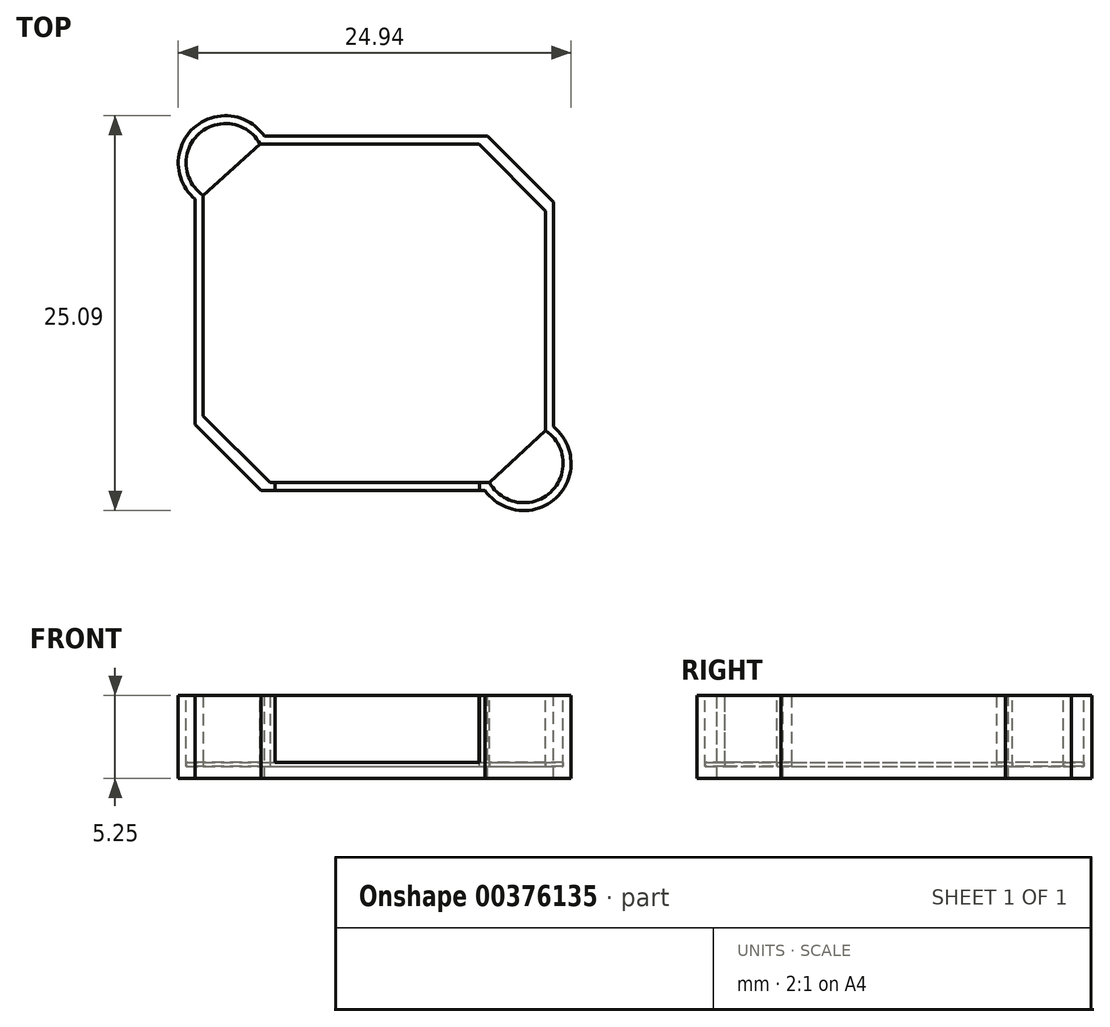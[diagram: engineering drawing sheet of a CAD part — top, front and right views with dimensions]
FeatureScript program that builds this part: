
annotation { "Feature Type Name" : "Feature", "Feature Type Description" : "" }
export const myFeature = defineFeature(function(context is Context, id is Id, definition is map)
    precondition{}
    {
        {
            var Q0;
            Q0=qCreatedBy(makeId("Top.planeOp"),FACE);
            var sketch = newSketch(context, id + "F0", { "sketchPlane" : qUnion([Q0])});
            skLineSegment(sketch, "E0.bottom", {"start": v(11.06, 7.36) * mm, "end": v(32.81, 7.36) * mm});
            skLineSegment(sketch, "E0.top", {"start": v(11.06, 28.86) * mm, "end": v(32.81, 28.86) * mm});
            skLineSegment(sketch, "E0.left", {"start": v(11.06, 7.36) * mm, "end": v(11.06, 28.86) * mm});
            skLineSegment(sketch, "E0.right", {"start": v(32.81, 7.36) * mm, "end": v(32.81, 28.86) * mm});
            skSolve(sketch);
        }
        {
            var Q0;
            Q0=makeQuery(id+"F0.imprint","IMPRINT",FACE,{"disambiguationData":[TD([[makeQuery(id+"F0.imprint","IMPRINT",EDGE,{"derivedFrom":sQuery(id+"F0.wireOp",EDGE,"E0.bottom")}),1.0]])]});
            extrude(context, id + "F1", {"entities" : qUnion([Q0]), "depth" : 6.5 * mm, "offsetDistance" : 25 * mm});
        }
        {
            var Q0;
            Q0=makeQuery(id+"F1.opExtrude","CAP_FACE",FACE,{"disambiguationData":[OSD([sQuery(id+"F0.wireOp",EDGE,"E0.bottom"),sQuery(id+"F0.wireOp",EDGE,"E0.top"),sQuery(id+"F0.wireOp",EDGE,"E0.left"),sQuery(id+"F0.wireOp",EDGE,"E0.right")])],"isStart":false});
            var sketch = newSketch(context, id + "F2", { "sketchPlane" : qUnion([Q0])});
            skCircle(sketch, "E1", {"center": v(12.48, 27.67) * mm, "radius": 2.5 * mm});
            skCircle(sketch, "E2", {"center": v(31.42, 8.58) * mm, "radius": 2.5 * mm});
            skSolve(sketch);
        }
        {
            var Q0;
            Q0 = qSketchRegion(id + "F2", true);
            var Q1;
            Q1=makeQuery(id+"F1.opExtrude","CAP_FACE",FACE,{"disambiguationData":[OSD([sQuery(id+"F0.wireOp",EDGE,"E0.bottom"),sQuery(id+"F0.wireOp",EDGE,"E0.top"),sQuery(id+"F0.wireOp",EDGE,"E0.left"),sQuery(id+"F0.wireOp",EDGE,"E0.right")])],"isStart":true});
            extrude(context, id + "F3", {"entities" : qUnion([Q0]), "operationType" : NewBodyOperationType.ADD, "endBound" : BoundingType.UP_TO_SURFACE, "oppositeDirection" : true, "endBoundEntityFace" : qUnion([Q1]), "depth" : 25 * mm});
        }
        {
            var Q0;
            {var subQ0=sQuery(id+"F0.wireOp",EDGE,"E0.right");var subQ1=sQuery(id+"F0.wireOp",EDGE,"E0.top");var subQ2=sQuery(id+"F0.wireOp",EDGE,"E0.left");var subQ3=sQuery(id+"F0.wireOp",EDGE,"E0.bottom");Q0=makeQuery(id+"F3.boolean.opBoolean","MERGE",FACE,{"derivedFrom":[makeQuery(id+"F1.opExtrude","CAP_FACE",FACE,{"disambiguationData":[OSD([subQ3,subQ1,subQ2,subQ0])],"isStart":false}),makeQuery(id+"F3.opExtrude","CAP_FACE",FACE,{"disambiguationData":[OSD([subQ3,subQ2,sQuery(id+"F2.wireOp",EDGE,"4af49626-d3c6-4b5d-b80f-25b6aeb158dc")])],"isStart":true}),makeQuery(id+"F3.opExtrude","CAP_FACE",FACE,{"disambiguationData":[OSD([subQ1,subQ0,sQuery(id+"F2.wireOp",EDGE,"7a161d0c-e22c-40a0-a662-b902da0d4264")])],"isStart":true})]});}
            var Q1;
            Q1=makeQuery(id+"F1.opExtrude","SWEPT_BODY",BODY,{"disambiguationData":[OSD([sQuery(id+"F0.wireOp",EDGE,"E0.bottom"),sQuery(id+"F0.wireOp",EDGE,"E0.top"),sQuery(id+"F0.wireOp",EDGE,"E0.left"),sQuery(id+"F0.wireOp",EDGE,"E0.right")])]});
            shell(context, id + "F4", {"entities" : qUnion([Q0]), "parts" : qUnion([Q1]), "thickness" : 0.5 * mm, "oppositeDirection" : true});
        }
        {
            var Q0;
            Q0=makeQuery(id+"F0.imprint","IMPRINT",FACE,{"disambiguationData":[TD([[makeQuery(id+"F0.imprint","IMPRINT",EDGE,{"derivedFrom":sQuery(id+"F0.wireOp",EDGE,"E0.bottom")}),1.0]])]});
            var sketch = newSketch(context, id + "F5", { "sketchPlane" : qUnion([Q0])});
            skCircle(sketch, "E3", {"center": v(21.94, 18.1) * mm, "radius": 6 * mm});
            skLineSegment(sketch, "E4", {"start": v(32.81, 18.1) * mm, "end": v(11.06, 18.1) * mm});
            skSolve(sketch);
        }
        {
            var Q0;
            Q0=makeQuery(id+"F3.boolean.opBoolean","MERGE",FACE,{"derivedFrom":[makeQuery(id+"F1.opExtrude","CAP_FACE",FACE,{"disambiguationData":[OSD([sQuery(id+"F0.wireOp",EDGE,"E0.bottom"),sQuery(id+"F0.wireOp",EDGE,"E0.top"),sQuery(id+"F0.wireOp",EDGE,"E0.left"),sQuery(id+"F0.wireOp",EDGE,"E0.right")])],"isStart":false}),makeQuery(id+"F3.opExtrude","CAP_FACE",FACE,{"disambiguationData":[OSD([sQuery(id+"F2.wireOp",EDGE,"E1")])],"isStart":true}),makeQuery(id+"F3.opExtrude","CAP_FACE",FACE,{"disambiguationData":[OSD([sQuery(id+"F2.wireOp",EDGE,"E2")])],"isStart":true})]});
            var sketch = newSketch(context, id + "F6", { "sketchPlane" : qUnion([Q0])});
            skLineSegment(sketch, "E5", {"start": v(32.81, 10.66) * mm, "end": v(32.81, 5.92) * mm});
            skLineSegment(sketch, "E6", {"start": v(32.81, 5.92) * mm, "end": v(37.54, 5.92) * mm});
            skLineSegment(sketch, "E7", {"start": v(37.54, 5.92) * mm, "end": v(37.54, 10.66) * mm});
            skLineSegment(sketch, "E8", {"start": v(37.54, 10.66) * mm, "end": v(32.81, 10.66) * mm});
            skLineSegment(sketch, "E9", {"start": v(32.81, 10.66) * mm, "end": v(32.81, 10.66) * mm});
            skSolve(sketch);
        }
        {
            var Q0;
            Q0=makeQuery(id+"F0.imprint","IMPRINT",FACE,{"disambiguationData":[TD([[makeQuery(id+"F0.imprint","IMPRINT",EDGE,{"derivedFrom":sQuery(id+"F0.wireOp",EDGE,"E0.bottom")}),1.0]])]});
            var sketch = newSketch(context, id + "F7", { "sketchPlane" : qUnion([Q0])});
            skLineSegment(sketch, "E10", {"start": v(11.06, 11.6) * mm, "end": v(15.3, 7.36) * mm});
            skLineSegment(sketch, "E11", {"start": v(11.06, 10.54) * mm, "end": v(14.24, 7.36) * mm});
            skLineSegment(sketch, "E12", {"start": v(11.06, 10.54) * mm, "end": v(11.06, 11.6) * mm});
            skLineSegment(sketch, "E13", {"start": v(14.24, 7.36) * mm, "end": v(15.3, 7.36) * mm});
            skLineSegment(sketch, "E14", {"start": v(28.57, 28.86) * mm, "end": v(32.81, 24.61) * mm});
            skLineSegment(sketch, "E15", {"start": v(29.63, 28.86) * mm, "end": v(32.81, 25.68) * mm});
            skSolve(sketch);
        }
        {
            var Q0;
            Q0 = qSketchRegion(id + "F7", true);
            var Q1;
            {var subQ0=sQuery(id+"F7.wireOp",EDGE,"E14");Q1=makeQuery(id+"F7.imprint","IMPRINT",FACE,{"disambiguationData":[TD([[makeQuery(id+"F7.imprint","IMPRINT",EDGE,{"derivedFrom":subQ0}),1.0]])]});}
            var Q2;
            Q2=makeQuery(id+"F3.boolean.opBoolean","MERGE",FACE,{"derivedFrom":[makeQuery(id+"F1.opExtrude","CAP_FACE",FACE,{"disambiguationData":[OSD([sQuery(id+"F0.wireOp",EDGE,"E0.bottom"),sQuery(id+"F0.wireOp",EDGE,"E0.top"),sQuery(id+"F0.wireOp",EDGE,"E0.left"),sQuery(id+"F0.wireOp",EDGE,"E0.right")])],"isStart":false}),makeQuery(id+"F3.opExtrude","CAP_FACE",FACE,{"disambiguationData":[OSD([sQuery(id+"F2.wireOp",EDGE,"E1")])],"isStart":true}),makeQuery(id+"F3.opExtrude","CAP_FACE",FACE,{"disambiguationData":[OSD([sQuery(id+"F2.wireOp",EDGE,"E2")])],"isStart":true})]});
            extrude(context, id + "F8", {"entities" : qUnion([Q0, Q1]), "operationType" : NewBodyOperationType.ADD, "endBound" : BoundingType.UP_TO_SURFACE, "endBoundEntityFace" : qUnion([Q2]), "depth" : 25 * mm});
        }
        {
            var Q0;
            {var subQ0=sQuery(id+"F2.wireOp",EDGE,"E2");var subQ1=sQuery(id+"F2.wireOp",EDGE,"E1");var subQ2=sQuery(id+"F0.wireOp",EDGE,"E0.right");var subQ3=sQuery(id+"F0.wireOp",EDGE,"E0.left");var subQ4=sQuery(id+"F0.wireOp",EDGE,"E0.top");var subQ5=sQuery(id+"F0.wireOp",EDGE,"E0.bottom");Q0=makeQuery(id+"F8.boolean.opBoolean","MERGE",FACE,{"derivedFrom":[makeQuery(id+"F3.boolean.opBoolean","MERGE",FACE,{"derivedFrom":[makeQuery(id+"F1.opExtrude","CAP_FACE",FACE,{"disambiguationData":[OSD([subQ5,subQ4,subQ3,subQ2])],"isStart":false}),makeQuery(id+"F3.opExtrude","CAP_FACE",FACE,{"disambiguationData":[OSD([subQ1])],"isStart":true}),makeQuery(id+"F3.opExtrude","CAP_FACE",FACE,{"disambiguationData":[OSD([subQ0])],"isStart":true})]}),makeQuery(id+"F8.opExtrude","CAP_FACE",FACE,{"disambiguationData":[OSD([subQ5,subQ4,subQ3,subQ2,subQ1,subQ0])],"isStart":false})]});}
            var sketch = newSketch(context, id + "F9", { "sketchPlane" : qUnion([Q0])});
            skLineSegment(sketch, "E16", {"start": v(11.06, 10.54) * mm, "end": v(10.56, 11.04) * mm});
            skLineSegment(sketch, "E17", {"start": v(10.56, 11.04) * mm, "end": v(10.56, 6.86) * mm});
            skLineSegment(sketch, "E18", {"start": v(10.56, 6.86) * mm, "end": v(14.74, 6.86) * mm});
            skLineSegment(sketch, "E19", {"start": v(14.74, 6.86) * mm, "end": v(14.24, 7.36) * mm});
            skLineSegment(sketch, "E20", {"start": v(14.24, 7.36) * mm, "end": v(11.06, 10.54) * mm});
            skLineSegment(sketch, "E21", {"start": v(33.31, 29.36) * mm, "end": v(29.13, 29.36) * mm});
            skLineSegment(sketch, "E22", {"start": v(29.13, 29.36) * mm, "end": v(29.63, 28.86) * mm});
            skLineSegment(sketch, "E23", {"start": v(29.63, 28.86) * mm, "end": v(32.81, 25.68) * mm});
            skLineSegment(sketch, "E24", {"start": v(32.81, 25.68) * mm, "end": v(33.31, 25.18) * mm});
            skLineSegment(sketch, "E25", {"start": v(33.31, 25.18) * mm, "end": v(33.31, 29.36) * mm});
            skSolve(sketch);
        }
        {
            var Q0;
            Q0 = qSketchRegion(id + "F9", true);
            var Q1;
            {var subQ15=sQuery(id+"F9.wireOp",EDGE,"E21");Q1=makeQuery(id+"F9.imprint","IMPRINT",FACE,{"disambiguationData":[TD([[makeQuery(id+"F9.imprint","IMPRINT",EDGE,{"derivedFrom":subQ15}),-1.0]])]});}
            var Q2;
            {var subQ0=sQuery(id+"F2.wireOp",EDGE,"E2");var subQ1=sQuery(id+"F0.wireOp",EDGE,"E0.bottom");var subQ2=sQuery(id+"F0.wireOp",EDGE,"E0.right");var subQ3=sQuery(id+"F0.wireOp",EDGE,"E0.left");var subQ4=sQuery(id+"F0.wireOp",EDGE,"E0.top");var subQ5=sQuery(id+"F2.wireOp",EDGE,"E1");Q2=makeQuery(id+"F3.boolean.opBoolean","MERGE",FACE,{"derivedFrom":[makeQuery(id+"F1.opExtrude","CAP_FACE",FACE,{"disambiguationData":[OSD([subQ1,subQ4,subQ3,subQ2])],"isStart":true}),makeQuery(id+"F3.opExtrude","CAP_FACE",FACE,{"disambiguationData":[OSD([subQ1,subQ4,subQ3,subQ2]),ownerDisambiguation([makeQuery(id+"F2.imprint","IMPRINT",EDGE,{"disambiguationData":[TD([[makeQuery(id+"F2.imprint","INTERSECT",VERTEX,{"derivedFrom":[makeQuery(id+"F1.opExtrude","CAP_EDGE",EDGE,{"disambiguationData":[OSD([subQ4])],"isStart":false}),subQ5]}),-1.0]])],"derivedFrom":subQ5})])],"isStart":false}),makeQuery(id+"F3.opExtrude","CAP_FACE",FACE,{"disambiguationData":[OSD([subQ1,subQ4,subQ3,subQ2]),ownerDisambiguation([makeQuery(id+"F2.imprint","IMPRINT",EDGE,{"disambiguationData":[TD([[makeQuery(id+"F2.imprint","INTERSECT",VERTEX,{"derivedFrom":[makeQuery(id+"F1.opExtrude","CAP_EDGE",EDGE,{"disambiguationData":[OSD([subQ1])],"isStart":false}),subQ0]}),1.0]])],"derivedFrom":subQ0})])],"isStart":false})]});}
            extrude(context, id + "F10", {"entities" : qUnion([Q0, Q1]), "operationType" : NewBodyOperationType.REMOVE, "endBound" : BoundingType.UP_TO_SURFACE, "oppositeDirection" : true, "endBoundEntityFace" : qUnion([Q2]), "depth" : 25 * mm, "offsetDistance" : 25 * mm});
        }
        {
            var Q0;
            Q0=makeQuery(id+"F1.opExtrude","SWEPT_BODY",BODY,{"disambiguationData":[OSD([sQuery(id+"F0.wireOp",EDGE,"E0.bottom"),sQuery(id+"F0.wireOp",EDGE,"E0.top"),sQuery(id+"F0.wireOp",EDGE,"E0.left"),sQuery(id+"F0.wireOp",EDGE,"E0.right")])]});
            transform(context, id + "F11", {"entities" : qUnion([Q0]), "transformType" : TransformType.TRANSLATION_3D, "dx" : 0 * mm, "dy" : 0 * mm, "dz" : 0 * mm, "makeCopy" : true});
        }
        {
            var Q0;
            {var subQ0=sQuery(id+"F0.wireOp",EDGE,"E0.right");var subQ1=sQuery(id+"F0.wireOp",EDGE,"E0.bottom");var subQ2=sQuery(id+"F0.wireOp",EDGE,"E0.top");var subQ3=sQuery(id+"F0.wireOp",EDGE,"E0.left");Q0=makeQuery(id+"F8.boolean.opBoolean","SPLIT",FACE,{"disambiguationData":[TD([makeQuery(id+"F4.opShell","OFFSET_FACE",FACE,{"disambiguationData":[OSD([sQuery(id+"F2.wireOp",EDGE,"E1")])]})])],"derivedFrom":makeQuery(id+"F4.opShell","OFFSET_FACE",FACE,{"disambiguationData":[OSD([subQ1,subQ2,subQ3,subQ0])]})});}
            var sketch = newSketch(context, id + "F12", { "sketchPlane" : qUnion([Q0])});
            skLineSegment(sketch, "E26", {"start": v(11.06, 25.6) * mm, "end": v(14.67, 28.86) * mm});
            skLineSegment(sketch, "E27", {"start": v(29.25, 7.36) * mm, "end": v(32.81, 10.66) * mm});
            skArc(sketch, "E28.0", {"start": v(32.81, 10.66) * mm, "mid": v(33.12, 6.75) * mm, "end": v(29.25, 7.36) * mm});
            skArc(sketch, "E29.0", {"start": v(11.06, 25.6) * mm, "mid": v(10.8, 29.52) * mm, "end": v(14.67, 28.86) * mm});
            skSolve(sketch);
        }
        {
            var Q0;
            Q0 = qSketchRegion(id + "F12", true);
            extrude(context, id + "F13", {"entities" : qUnion([Q0]), "depth" : 3 * mm, "offsetDistance" : 25 * mm});
        }
        {
            var Q0;
            {var subQ0=sQuery(id+"F0.wireOp",EDGE,"E0.right");var subQ1=sQuery(id+"F0.wireOp",EDGE,"E0.bottom");var subQ2=sQuery(id+"F0.wireOp",EDGE,"E0.top");var subQ3=sQuery(id+"F0.wireOp",EDGE,"E0.left");Q0=makeQuery(id+"F8.boolean.opBoolean","SPLIT",FACE,{"disambiguationData":[TD([makeQuery(id+"F4.opShell","OFFSET_FACE",FACE,{"disambiguationData":[OSD([sQuery(id+"F2.wireOp",EDGE,"E1")])]})])],"derivedFrom":makeQuery(id+"F4.opShell","OFFSET_FACE",FACE,{"disambiguationData":[OSD([subQ1,subQ2,subQ3,subQ0])]})});}
            extrude(context, id + "F14", {"entities" : qUnion([Q0]), "depth" : .25 * mm, "offsetDistance" : 25 * mm});
        }
        {
            var Q0;
            {var subQ2=sQuery(id+"F0.wireOp",EDGE,"E0.bottom");var subQ3=makeQuery(id+"F1.opExtrude","CAP_EDGE",EDGE,{"disambiguationData":[OSD([subQ2])],"isStart":false});Q0=makeQuery(id+"F6.imprint","IMPRINT",FACE,{"disambiguationData":[TD([[makeQuery(id+"F6.imprint","IMPRINT",EDGE,{"derivedFrom":subQ3}),1.0]])]});}
            var sketch = newSketch(context, id + "F15", { "sketchPlane" : qUnion([Q0])});
            skLineSegment(sketch, "E30.0.0", {"start": v(32.81, 10.66) * mm, "end": v(33.59, 10.66) * mm});
            skArc(sketch, "E30.0.1", {"start": v(33.59, 10.66) * mm, "mid": v(33.45, 10.8) * mm, "end": v(33.31, 10.91) * mm});
            skLineSegment(sketch, "E30.0.2", {"start": v(33.31, 10.91) * mm, "end": v(33.31, 29.36) * mm});
            skLineSegment(sketch, "E30.0.3", {"start": v(33.31, 29.36) * mm, "end": v(14.95, 29.36) * mm});
            skArc(sketch, "E30.0.4", {"start": v(14.95, 29.36) * mm, "mid": v(10.46, 29.88) * mm, "end": v(10.56, 25.36) * mm});
            skLineSegment(sketch, "E30.0.5", {"start": v(10.56, 25.36) * mm, "end": v(10.56, 6.86) * mm});
            skLineSegment(sketch, "E30.0.6", {"start": v(10.56, 6.86) * mm, "end": v(28.97, 6.86) * mm});
            skArc(sketch, "E30.0.7", {"start": v(28.97, 6.86) * mm, "mid": v(30.71, 5.67) * mm, "end": v(32.81, 5.92) * mm});
            skLineSegment(sketch, "E30.0.8", {"start": v(32.81, 5.92) * mm, "end": v(32.81, 6.5) * mm});
            skArc(sketch, "E30.0.9", {"start": v(32.81, 6.5) * mm, "mid": v(30.84, 6.15) * mm, "end": v(29.25, 7.36) * mm});
            skLineSegment(sketch, "E30.0.10", {"start": v(29.25, 7.36) * mm, "end": v(11.06, 7.36) * mm});
            skLineSegment(sketch, "E30.0.11", {"start": v(11.06, 7.36) * mm, "end": v(11.06, 25.6) * mm});
            skArc(sketch, "E30.0.12", {"start": v(11.06, 25.6) * mm, "mid": v(10.8, 29.52) * mm, "end": v(14.67, 28.86) * mm});
            skLineSegment(sketch, "E30.0.13", {"start": v(14.67, 28.86) * mm, "end": v(32.81, 28.86) * mm});
            skLineSegment(sketch, "E30.0.14", {"start": v(32.81, 28.86) * mm, "end": v(32.81, 10.66) * mm});
            skLineSegment(sketch, "E31", {"start": v(32.81, 24.2) * mm, "end": v(33.31, 24.2) * mm});
            skLineSegment(sketch, "E32", {"start": v(32.81, 11.36) * mm, "end": v(33.31, 11.36) * mm});
            skLineSegment(sketch, "E33", {"start": v(15.64, 7.36) * mm, "end": v(15.64, 6.86) * mm});
            skLineSegment(sketch, "E34", {"start": v(28.6, 7.36) * mm, "end": v(28.6, 6.86) * mm});
            skSolve(sketch);
        }
        {
            var Q0;
            {var subQ0=sQuery(id+"F15.wireOp",EDGE,"E31");Q0=makeQuery(id+"F15.imprint","IMPRINT",FACE,{"disambiguationData":[TD([[makeQuery(id+"F15.imprint","IMPRINT",EDGE,{"derivedFrom":subQ0}),-1.0]])]});}
            extrude(context, id + "F16", {"entities" : qUnion([Q0]), "operationType" : NewBodyOperationType.REMOVE, "oppositeDirection" : true, "depth" : 2 * mm, "offsetDistance" : 25 * mm});
        }
        {
            var Q0;
            Q0=makeQuery(id+"F13.opExtrude","CAP_FACE",FACE,{"disambiguationData":[OSD([sQuery(id+"F12.wireOp",EDGE,"E26"),sQuery(id+"F12.wireOp",EDGE,"E29.0")])],"isStart":false});
            var Q1;
            Q1=makeQuery(id+"F13.opExtrude","CAP_FACE",FACE,{"disambiguationData":[OSD([sQuery(id+"F12.wireOp",EDGE,"E27"),sQuery(id+"F12.wireOp",EDGE,"E28.0")])],"isStart":false});
            var Q2;
            Q2=makeQuery(id+"F14.opExtrude","CAP_FACE",FACE,{"disambiguationData":[OSD([sQuery(id+"F0.wireOp",EDGE,"E0.bottom"),sQuery(id+"F0.wireOp",EDGE,"E0.top"),sQuery(id+"F0.wireOp",EDGE,"E0.left"),sQuery(id+"F0.wireOp",EDGE,"E0.right")])],"isStart":false});
            extrude(context, id + "F17", {"entities" : qUnion([Q0, Q1]), "operationType" : NewBodyOperationType.REMOVE, "endBound" : BoundingType.UP_TO_SURFACE, "oppositeDirection" : true, "depth" : 25 * mm, "endBoundEntityFace" : qUnion([Q2]), "offsetDistance" : 25 * mm});
        }
        {
            var Q0;
            {var subQ0=sQuery(id+"F15.wireOp",EDGE,"E33");Q0=makeQuery(id+"F15.imprint","IMPRINT",FACE,{"disambiguationData":[TD([[makeQuery(id+"F15.imprint","IMPRINT",EDGE,{"derivedFrom":subQ0}),1.0]])]});}
            var Q1;
            {var subQ0=sQuery(id+"F0.wireOp",EDGE,"E0.right");var subQ1=sQuery(id+"F0.wireOp",EDGE,"E0.left");var subQ2=sQuery(id+"F0.wireOp",EDGE,"E0.top");var subQ3=sQuery(id+"F0.wireOp",EDGE,"E0.bottom");Q1=makeQuery(id+"F17.boolean.opBoolean","MERGE",FACE,{"derivedFrom":[makeQuery(id+"F14.opExtrude","CAP_FACE",FACE,{"disambiguationData":[OSD([subQ3,subQ2,subQ1,subQ0])],"isStart":false}),makeQuery(id+"F17.opExtrude","CAP_FACE",FACE,{"disambiguationData":[OSD([subQ3,subQ2,subQ1,subQ0]),OD(0.0)],"isStart":false}),makeQuery(id+"F17.opExtrude","CAP_FACE",FACE,{"disambiguationData":[OSD([subQ3,subQ2,subQ1,subQ0]),OD(1.0)],"isStart":false})]});}
            extrude(context, id + "F18", {"entities" : qUnion([Q0]), "operationType" : NewBodyOperationType.REMOVE, "endBound" : BoundingType.UP_TO_SURFACE, "oppositeDirection" : true, "depth" : 25 * mm, "endBoundEntityFace" : qUnion([Q1]), "offsetDistance" : 25 * mm});
        }
        {
            var Q0;
            {var subQ0=sQuery(id+"F0.wireOp",EDGE,"E0.right");var subQ1=sQuery(id+"F0.wireOp",EDGE,"E0.left");var subQ2=sQuery(id+"F0.wireOp",EDGE,"E0.top");var subQ3=sQuery(id+"F0.wireOp",EDGE,"E0.bottom");Q0=makeQuery(id+"F3.boolean.opBoolean","MERGE",FACE,{"derivedFrom":[makeQuery(id+"F1.opExtrude","CAP_FACE",FACE,{"disambiguationData":[OSD([subQ3,subQ2,subQ1,subQ0])],"isStart":true}),makeQuery(id+"F3.opExtrude","CAP_FACE",FACE,{"disambiguationData":[OSD([subQ3,subQ2,subQ1,subQ0]),OD(0.0)],"isStart":false}),makeQuery(id+"F3.opExtrude","CAP_FACE",FACE,{"disambiguationData":[OSD([subQ3,subQ2,subQ1,subQ0]),OD(1.0)],"isStart":false})]});}
            extrude(context, id + "F19", {"entities" : qUnion([Q0]), "operationType" : NewBodyOperationType.ADD, "depth" : 0.25 * mm, "offsetDistance" : 25 * mm});
        }
        {
            var Q0;
            {var subQ0=sQuery(id+"F0.wireOp",EDGE,"E0.right");var subQ1=sQuery(id+"F0.wireOp",EDGE,"E0.top");var subQ2=sQuery(id+"F0.wireOp",EDGE,"E0.bottom");var subQ3=sQuery(id+"F0.wireOp",EDGE,"E0.left");var subQ4=sQuery(id+"F2.wireOp",EDGE,"E1");var subQ5=sQuery(id+"F2.wireOp",EDGE,"E2");Q0=makeQuery(id+"F18.boolean.opBoolean","SPLIT",FACE,{"disambiguationData":[TD([makeQuery(id+"F1.opExtrude","SWEPT_FACE",FACE,{"disambiguationData":[OSD([subQ1])]})])],"derivedFrom":makeQuery(id+"F8.boolean.opBoolean","MERGE",FACE,{"derivedFrom":[makeQuery(id+"F3.boolean.opBoolean","MERGE",FACE,{"derivedFrom":[makeQuery(id+"F1.opExtrude","CAP_FACE",FACE,{"disambiguationData":[OSD([subQ2,subQ1,subQ3,subQ0])],"isStart":false}),makeQuery(id+"F3.opExtrude","CAP_FACE",FACE,{"disambiguationData":[OSD([subQ4])],"isStart":true}),makeQuery(id+"F3.opExtrude","CAP_FACE",FACE,{"disambiguationData":[OSD([subQ5])],"isStart":true})]}),makeQuery(id+"F8.opExtrude","CAP_FACE",FACE,{"disambiguationData":[OSD([subQ2,subQ1,subQ3,subQ0,subQ4,subQ5]),OD(0.0)],"isStart":false}),makeQuery(id+"F8.opExtrude","CAP_FACE",FACE,{"disambiguationData":[OSD([subQ2,subQ1,subQ3,subQ0,subQ4,subQ5]),OD(1.0)],"isStart":false})]})});}
            var Q1;
            {var subQ1=sQuery(id+"F15.wireOp",EDGE,"E30.0.7");Q1=makeQuery(id+"F15.imprint","IMPRINT",FACE,{"disambiguationData":[TD([[makeQuery(id+"F15.imprint","IMPRINT",EDGE,{"derivedFrom":subQ1}),1.0]])]});}
            var Q2;
            {var subQ0=sQuery(id+"F6.wireOp",EDGE,"E5");var subQ1=sQuery(id+"F2.wireOp",EDGE,"E2");var subQ4=makeQuery(id+"F4.opShell","OFFSET_EDGE",EDGE,{"disambiguationData":[OSD([subQ1])]});var subQ5=makeQuery(id+"F6.imprint","INTERSECT",VERTEX,{"derivedFrom":[subQ4,subQ0]});Q2=makeQuery(id+"F6.imprint","IMPRINT",FACE,{"disambiguationData":[TD([[makeQuery(id+"F6.imprint","IMPRINT",EDGE,{"disambiguationData":[TD([[subQ5,-1.0]])],"derivedFrom":subQ0}),1.0]])]});}
            var Q3;
            {var subQ4=sQuery(id+"F15.wireOp",EDGE,"E30.0.0");Q3=makeQuery(id+"F15.imprint","IMPRINT",FACE,{"disambiguationData":[TD([[makeQuery(id+"F15.imprint","IMPRINT",EDGE,{"derivedFrom":subQ4}),-1.0]])]});}
            var Q4;
            Q4=makeQuery(id+"F16.boolean.opBoolean","COPY",FACE,{"derivedFrom":makeQuery(id+"F16.opExtrude","CAP_FACE",FACE,{"disambiguationData":[OSD([sQuery(id+"F15.wireOp",EDGE,"E30.0.2"),sQuery(id+"F15.wireOp",EDGE,"E30.0.14"),sQuery(id+"F15.wireOp",EDGE,"E31"),sQuery(id+"F15.wireOp",EDGE,"E32")])],"isStart":false})});
            extrude(context, id + "F20", {"entities" : qUnion([Q0, Q1, Q2, Q3]), "operationType" : NewBodyOperationType.REMOVE, "endBound" : BoundingType.UP_TO_SURFACE, "oppositeDirection" : true, "depth" : 25 * mm, "endBoundEntityFace" : qUnion([Q4]), "offsetDistance" : 25 * mm});
        }
    });
